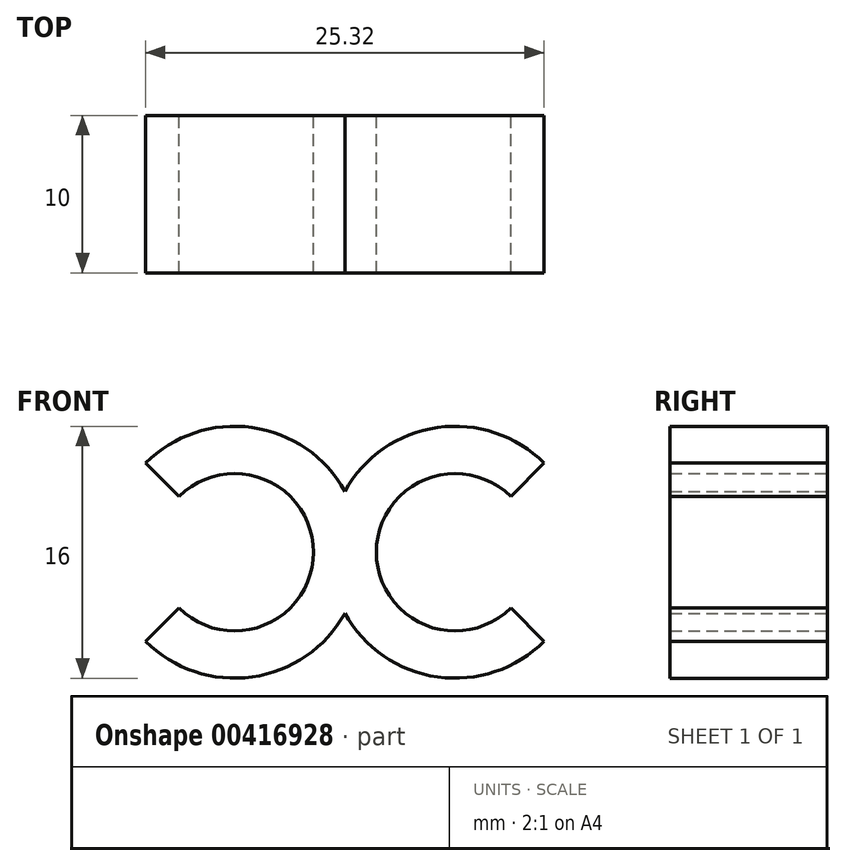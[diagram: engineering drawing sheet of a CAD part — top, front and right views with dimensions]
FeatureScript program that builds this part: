
annotation { "Feature Type Name" : "Feature", "Feature Type Description" : "" }
export const myFeature = defineFeature(function(context is Context, id is Id, definition is map)
    precondition{}
    {
        {
            var Q0;
            Q0=qCreatedBy(makeId("Front.planeOp"),FACE);
            var sketch = newSketch(context, id + "F0", { "sketchPlane" : qUnion([Q0])});
            skArc(sketch, "E0", {"start": v(-10.54, -3.54) * mm, "mid": v(-2, 0) * mm, "end": v(-10.54, 3.54) * mm});
            skArc(sketch, "E1", {"start": v(-12.66, -5.66) * mm, "mid": v(-5.88, -7.92) * mm, "end": v(0, -3.87) * mm});
            skLineSegment(sketch, "E2", {"start": v(-10.54, 3.54) * mm, "end": v(-12.66, 5.66) * mm});
            skLineSegment(sketch, "E3", {"start": v(-10.54, -3.54) * mm, "end": v(-12.66, -5.66) * mm});
            skLineSegment(sketch, "E4.MirrorCS", {"start": v(10.54, 3.54) * mm, "end": v(12.66, 5.66) * mm});
            skLineSegment(sketch, "E5.MirrorCS", {"start": v(10.54, -3.54) * mm, "end": v(12.66, -5.66) * mm});
            skArc(sketch, "E6.MirrorCS", {"start": v(10.54, -3.54) * mm, "mid": v(2, 0) * mm, "end": v(10.54, 3.54) * mm});
            skArc(sketch, "E7.MirrorCS", {"start": v(12.66, -5.66) * mm, "mid": v(5.88, -7.92) * mm, "end": v(0, -3.87) * mm});
            skArc(sketch, "E8.trimOffspring", {"start": v(0, 3.87) * mm, "mid": v(5.88, 7.92) * mm, "end": v(12.66, 5.66) * mm});
            skArc(sketch, "E9.trimOffspring", {"start": v(0, 3.87) * mm, "mid": v(-5.88, 7.92) * mm, "end": v(-12.66, 5.66) * mm});
            skSolve(sketch);
        }
        {
            var Q0;
            Q0 = qSketchRegion(id + "F0", true);
            extrude(context, id + "F1", {"entities" : qUnion([Q0]), "depth" : 10 * mm});
        }
    });
